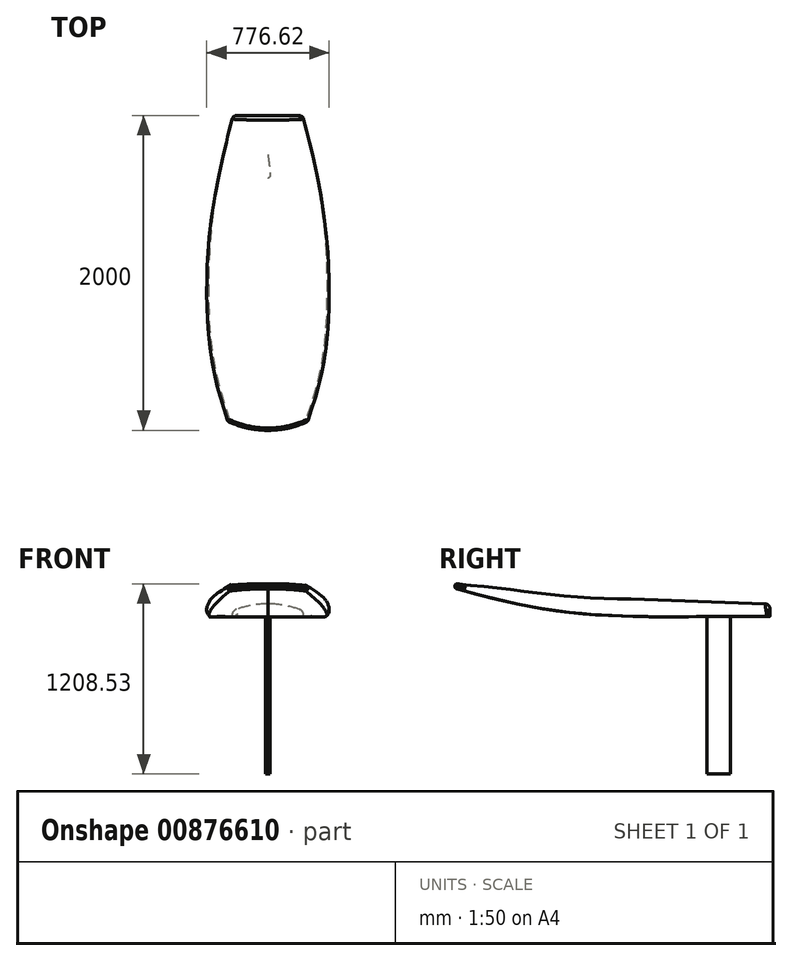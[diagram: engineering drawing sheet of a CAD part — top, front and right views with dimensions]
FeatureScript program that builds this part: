
annotation { "Feature Type Name" : "Feature", "Feature Type Description" : "" }
export const myFeature = defineFeature(function(context is Context, id is Id, definition is map)
    precondition{}
    {
        {
            var Q0;
            Q0=qCreatedBy(makeId("Right.planeOp"),FACE);
            var sketch = newSketch(context, id + "F0", { "sketchPlane" : qUnion([Q0])});
            skLineSegment(sketch, "E0", {"start": v(400, 0) * mm, "end": v(-400, 0) * mm, "construction": true});
            skLineSegment(sketch, "E1", {"start": v(-1600, 0) * mm, "end": v(-1600, 210) * mm, "construction": true});
            skLineSegment(sketch, "E2", {"start": v(-1600, 210) * mm, "end": v(400, 210) * mm, "construction": true});
            skLineSegment(sketch, "E3", {"start": v(400, 210) * mm, "end": v(400, 0) * mm, "construction": true});
            skArc(sketch, "E4", {"start": v(-1600, 180) * mm, "mid": v(-1006.71, 45.25) * mm, "end": v(-400, 0) * mm});
            skLineSegment(sketch, "E5", {"start": v(0, 0) * mm, "end": v(0, -1000) * mm});
            skLineSegment(sketch, "E6", {"start": v(150, 0) * mm, "end": v(150, -1000) * mm});
            skLineSegment(sketch, "E7", {"start": v(-200, -1000) * mm, "end": v(600, -1000) * mm});
            skLineSegment(sketch, "E8", {"start": v(400, 80) * mm, "end": v(-290.38, 105) * mm});
            skPoint(sketch, "E8.endSnap0", {"position": v(400, 105) * mm});
            skArc(sketch, "E9", {"start": v(-1600, 210) * mm, "mid": v(-946.34, 143.15) * mm, "end": v(-290.38, 105) * mm});
            skPoint(sketch, "E10", {"position": v(200, 0) * mm});
            skPoint(sketch, "E11", {"position": v(-200, 0) * mm});
            skPoint(sketch, "E12", {"position": v(-600, 4.9) * mm});
            skPoint(sketch, "E13", {"position": v(-800, 19.6) * mm});
            skPoint(sketch, "E14", {"position": v(-1000, 44.25) * mm});
            skPoint(sketch, "E15", {"position": v(-1200, 79) * mm});
            skPoint(sketch, "E16", {"position": v(-1400, 124.13) * mm});
            skLineSegment(sketch, "E17", {"start": v(400, 10) * mm, "end": v(-421.1, 30) * mm, "construction": true});
            skArc(sketch, "E18", {"start": v(-1600, 195) * mm, "mid": v(-1015.29, 78.66) * mm, "end": v(-421.1, 30) * mm, "construction": true});
            skLineSegment(sketch, "E19", {"start": v(400, 70) * mm, "end": v(-600, 93.11) * mm});
            skArc(sketch, "E20", {"start": v(-600, 93.11) * mm, "mid": v(-1101.55, 81.85) * mm, "end": v(-1600, 25) * mm});
            skPoint(sketch, "E21", {"position": v(-400, 108.97) * mm});
            skSolve(sketch);
        }
        {
            var Q0;
            Q0=qCreatedBy(makeId("Top.planeOp"),FACE);
            var sketch = newSketch(context, id + "F1", { "sketchPlane" : qUnion([Q0])});
            skLineSegment(sketch, "E22.left", {"start": v(0, 400) * mm, "end": v(0, -1600) * mm});
            skLineSegment(sketch, "E23.bottom", {"start": v(375, -1600) * mm, "end": v(-375, -1600) * mm});
            skLineSegment(sketch, "E23.top", {"start": v(375, 400) * mm, "end": v(-375, 400) * mm});
            skLineSegment(sketch, "E23.left", {"start": v(375, -1600) * mm, "end": v(375, 400) * mm});
            skLineSegment(sketch, "E23.right", {"start": v(-375, -1600) * mm, "end": v(-375, 400) * mm});
            skFitSpline(sketch, "E24", {"points": [v(220, 400) * mm, v(350, -250) * mm, v(350, -1100) * mm, v(220, -1600) * mm], "startDerivative": vector(542.74, -2261.4) * mm, "endDerivative": vector(-470.53, -717.24) * mm});
            skFitSpline(sketch, "E25", {"points": [v(0, 150) * mm, v(-12, 40) * mm, v(-10, 12.5) * mm, v(0, 0) * mm], "startDerivative": vector(-33.83, -253.74) * mm, "endDerivative": vector(59.3, -29.65) * mm});
            skArc(sketch, "E26", {"start": v(0, -1600) * mm, "mid": v(198.71, -1566.14) * mm, "end": v(375, -1468.37) * mm});
            skSolve(sketch);
        }
        {
            var Q0;
            Q0=sQuery(id+"F1.wireOp",EDGE,"E23.top");
            cPoint(context, id + "F2", {"entities" : qUnion([Q0]), "parameter" : 0.5});
        }
        {
            var Q0;
            Q0 = qCreatedBy(id + "F2" ,VERTEX);
            var Q1;
            Q1=qCreatedBy(makeId("Front.planeOp"),FACE);
            cPlane(context, id + "F3", {"entities" : qUnion([Q0, Q1]), "cplaneType" : CPlaneType.PLANE_POINT, "offset" : 25 * mm, "width" : 150 * mm, "height" : 150 * mm});
        }
        {
            var Q0;
            Q0=qCreatedBy(makeId("Front.planeOp"),FACE);
            var Q1;
            Q1=sQuery(id+"F0.wireOp",VERTEX,"E5.start");
            cPlane(context, id + "F4", {"entities" : qUnion([Q0, Q1]), "cplaneType" : CPlaneType.PLANE_POINT, "offset" : 25 * mm, "width" : 150 * mm, "height" : 150 * mm});
        }
        {
            var Q0;
            Q0=qCreatedBy(makeId("Front.planeOp"),FACE);
            var Q1;
            Q1=sQuery(id+"F0.wireOp",VERTEX,"E4.end");
            cPlane(context, id + "F5", {"entities" : qUnion([Q0, Q1]), "cplaneType" : CPlaneType.PLANE_POINT, "offset" : 25 * mm, "width" : 150 * mm, "height" : 150 * mm});
        }
        {
            var Q0;
            Q0=qCreatedBy(makeId("Front.planeOp"),FACE);
            var Q1;
            Q1=sQuery(id+"F0.wireOp",VERTEX,"E13");
            cPlane(context, id + "F6", {"entities" : qUnion([Q0, Q1]), "cplaneType" : CPlaneType.PLANE_POINT, "offset" : 25 * mm, "width" : 150 * mm, "height" : 150 * mm});
        }
        {
            var Q0;
            Q0=qCreatedBy(makeId("Front.planeOp"),FACE);
            var Q1;
            Q1=sQuery(id+"F0.wireOp",VERTEX,"E15");
            cPlane(context, id + "F7", {"entities" : qUnion([Q0, Q1]), "cplaneType" : CPlaneType.PLANE_POINT, "offset" : 25 * mm, "width" : 150 * mm, "height" : 150 * mm});
        }
        {
            var Q0;
            Q0=sQuery(id+"F0.wireOp",VERTEX,"E4.start");
            var Q1;
            Q1=qCreatedBy(makeId("Front.planeOp"),FACE);
            cPlane(context, id + "F8", {"entities" : qUnion([Q0, Q1]), "cplaneType" : CPlaneType.PLANE_POINT, "offset" : 25 * mm, "width" : 150 * mm, "height" : 150 * mm});
        }
        {
            var Q0;
            Q0=qCreatedBy(id+"F3.planeOp",FACE);
            var sketch = newSketch(context, id + "F9", { "sketchPlane" : qUnion([Q0])});
            skLineSegment(sketch, "E27", {"start": v(0, 0) * mm, "end": v(220, 0) * mm});
            skArc(sketch, "E28", {"start": v(199.15, 42.62) * mm, "mid": v(101.31, 70.57) * mm, "end": v(0, 80) * mm});
            skArc(sketch, "E29", {"start": v(220, 0) * mm, "mid": v(217.9, 25.38) * mm, "end": v(199.15, 42.62) * mm});
            skLineSegment(sketch, "E30", {"start": v(0, 0) * mm, "end": v(0, 80) * mm});
            skLineSegment(sketch, "E31", {"start": v(186.46, 10) * mm, "end": v(0, 10) * mm, "construction": true});
            skArc(sketch, "E32", {"start": v(0, 0) * mm, "mid": v(35, 35) * mm, "end": v(0, 70) * mm, "construction": true});
            skSolve(sketch);
        }
        {
            var Q0;
            Q0=qCreatedBy(id+"F4.planeOp",FACE);
            var sketch = newSketch(context, id + "F10", { "sketchPlane" : qUnion([Q0])});
            skLineSegment(sketch, "E33", {"start": v(0, 0) * mm, "end": v(310.81, 0) * mm});
            skArc(sketch, "E34", {"start": v(310.81, 0) * mm, "mid": v(312.98, 35.1) * mm, "end": v(286.37, 58.1) * mm});
            skArc(sketch, "E35", {"start": v(286.37, 58.1) * mm, "mid": v(144.33, 85.35) * mm, "end": v(0, 94.48) * mm});
            skLineSegment(sketch, "E36", {"start": v(0, 0) * mm, "end": v(0, 94.48) * mm});
            skLineSegment(sketch, "E37", {"start": v(276.46, 19.74) * mm, "end": v(0, 19.74) * mm, "construction": true});
            skArc(sketch, "E38", {"start": v(0, 79.24) * mm, "mid": v(39.62, 39.62) * mm, "end": v(0, 0) * mm, "construction": true});
            skSolve(sketch);
        }
        {
            var Q0;
            Q0=qCreatedBy(id+"F5.planeOp",FACE);
            var sketch = newSketch(context, id + "F11", { "sketchPlane" : qUnion([Q0])});
            skLineSegment(sketch, "E39", {"start": v(0, 0) * mm, "end": v(364.34, 0) * mm});
            skArc(sketch, "E40", {"start": v(364.34, 0) * mm, "mid": v(373.43, 43.18) * mm, "end": v(340.66, 72.74) * mm});
            skArc(sketch, "E41", {"start": v(340.66, 72.74) * mm, "mid": v(171.3, 99.89) * mm, "end": v(0, 108.97) * mm});
            skLineSegment(sketch, "E42", {"start": v(0, 0) * mm, "end": v(0, 108.97) * mm});
            skLineSegment(sketch, "E43", {"start": v(331.36, 29.49) * mm, "end": v(0, 29.49) * mm, "construction": true});
            skArc(sketch, "E44", {"start": v(0, 0) * mm, "mid": v(44.24, 44.24) * mm, "end": v(0, 88.49) * mm, "construction": true});
            skSolve(sketch);
        }
        {
            var Q0;
            Q0=qCreatedBy(id+"F6.planeOp",FACE);
            var sketch = newSketch(context, id + "F12", { "sketchPlane" : qUnion([Q0])});
            skLineSegment(sketch, "E45", {"start": v(0, 19.6) * mm, "end": v(373.23, 19.6) * mm});
            skLineSegment(sketch, "E46", {"start": v(373.23, 19.6) * mm, "end": v(373.23, 0) * mm, "construction": true});
            skArc(sketch, "E47", {"start": v(346.6, 99.7) * mm, "mid": v(173.7, 117.5) * mm, "end": v(0, 123.45) * mm});
            skLineSegment(sketch, "E48", {"start": v(340.18, 53.09) * mm, "end": v(0, 53.09) * mm, "construction": true});
            skLineSegment(sketch, "E49", {"start": v(0, 19.6) * mm, "end": v(0, 123.45) * mm});
            skArc(sketch, "E50", {"start": v(373.23, 19.6) * mm, "mid": v(384.82, 67.94) * mm, "end": v(346.6, 99.7) * mm});
            skArc(sketch, "E51", {"start": v(0, 0) * mm, "mid": v(47.05, 47.05) * mm, "end": v(0, 94.1) * mm, "construction": true});
            skSolve(sketch);
        }
        {
            var Q0;
            Q0=qCreatedBy(id+"F7.planeOp",FACE);
            var sketch = newSketch(context, id + "F13", { "sketchPlane" : qUnion([Q0])});
            skLineSegment(sketch, "E52", {"start": v(0, 79) * mm, "end": v(335.21, 79) * mm});
            skArc(sketch, "E53", {"start": v(335.21, 79) * mm, "mid": v(347.66, 117.93) * mm, "end": v(316.8, 144.7) * mm});
            skArc(sketch, "E54", {"start": v(316.8, 144.7) * mm, "mid": v(158.74, 160.42) * mm, "end": v(0, 165.66) * mm});
            skLineSegment(sketch, "E55", {"start": v(0, 79) * mm, "end": v(0, 165.66) * mm});
            skArc(sketch, "E56", {"start": v(0, 0) * mm, "mid": v(37.13, 37.13) * mm, "end": v(0, 74.26) * mm, "construction": true});
            skLineSegment(sketch, "E57", {"start": v(311.9, 107.9) * mm, "end": v(0, 107.9) * mm, "construction": true});
            skLineSegment(sketch, "E58", {"start": v(335.21, 79) * mm, "end": v(335.21, 0) * mm, "construction": true});
            skSolve(sketch);
        }
        {
            var Q0;
            Q0=qCreatedBy(id+"F8.planeOp",FACE);
            var sketch = newSketch(context, id + "F14", { "sketchPlane" : qUnion([Q0])});
            skLineSegment(sketch, "E59", {"start": v(0, 180) * mm, "end": v(220, 180) * mm});
            skLineSegment(sketch, "E60", {"start": v(220, 180) * mm, "end": v(220, 0) * mm, "construction": true});
            skLineSegment(sketch, "E61", {"start": v(0, 210) * mm, "end": v(0, 180) * mm});
            skLineSegment(sketch, "E62", {"start": v(0, 210) * mm, "end": v(220, 210) * mm});
            skArc(sketch, "E63", {"start": v(220, 180) * mm, "mid": v(235, 195) * mm, "end": v(220, 210) * mm});
            skSolve(sketch);
        }
        {
            var Q0;
            Q0=sQuery(id+"F1.wireOp",EDGE,"E24");
            var Q1;
            Q1=makeQuery(id+"F9.imprint","IMPRINT",FACE,{"disambiguationData":[TD([[makeQuery(id+"F9.imprint","IMPRINT",EDGE,{"derivedFrom":sQuery(id+"F9.wireOp",EDGE,"E27")}),1.0]])]});
            var Q2;
            Q2=makeQuery(id+"F10.imprint","IMPRINT",FACE,{"disambiguationData":[TD([[makeQuery(id+"F10.imprint","IMPRINT",EDGE,{"derivedFrom":sQuery(id+"F10.wireOp",EDGE,"E33")}),1.0]])]});
            var Q3;
            Q3=makeQuery(id+"F11.imprint","IMPRINT",FACE,{"disambiguationData":[TD([[makeQuery(id+"F11.imprint","IMPRINT",EDGE,{"derivedFrom":sQuery(id+"F11.wireOp",EDGE,"E39")}),1.0]])]});
            var Q4;
            Q4=makeQuery(id+"F12.imprint","IMPRINT",FACE,{"disambiguationData":[TD([[makeQuery(id+"F12.imprint","IMPRINT",EDGE,{"derivedFrom":sQuery(id+"F12.wireOp",EDGE,"E45")}),1.0]])]});
            var Q5;
            Q5=makeQuery(id+"F13.imprint","IMPRINT",FACE,{"disambiguationData":[TD([[makeQuery(id+"F13.imprint","IMPRINT",EDGE,{"derivedFrom":sQuery(id+"F13.wireOp",EDGE,"E52")}),1.0]])]});
            var Q6;
            Q6=makeQuery(id+"F14.imprint","IMPRINT",FACE,{"disambiguationData":[TD([[makeQuery(id+"F14.imprint","IMPRINT",EDGE,{"derivedFrom":sQuery(id+"F14.wireOp",EDGE,"E59")}),1.0]])]});
            var Q7;
            Q7 = qConstructionFilter(qBodyType(qCreatedBy(id + "F9" ,EDGE), BodyType.WIRE), ConstructionObject.NO);
            var Q8;
            Q8 = qConstructionFilter(qBodyType(qCreatedBy(id + "F10" ,EDGE), BodyType.WIRE), ConstructionObject.NO);
            var Q9;
            Q9 = qConstructionFilter(qBodyType(qCreatedBy(id + "F11" ,EDGE), BodyType.WIRE), ConstructionObject.NO);
            var Q10;
            Q10 = qConstructionFilter(qBodyType(qCreatedBy(id + "F12" ,EDGE), BodyType.WIRE), ConstructionObject.NO);
            var Q11;
            Q11 = qConstructionFilter(qBodyType(qCreatedBy(id + "F13" ,EDGE), BodyType.WIRE), ConstructionObject.NO);
            var Q12;
            Q12 = qConstructionFilter(qBodyType(qCreatedBy(id + "F14" ,EDGE), BodyType.WIRE), ConstructionObject.NO);
            var Q13;
            Q13=sQuery(id+"F1.wireOp",VERTEX,"E24.start");
            var Q14;
            Q14=sQuery(id+"F10.wireOp",VERTEX,"E33.end");
            var Q15;
            Q15=sQuery(id+"F11.wireOp",VERTEX,"E39.end");
            var Q16;
            Q16=sQuery(id+"F12.wireOp",VERTEX,"E45.end");
            var Q17;
            Q17=sQuery(id+"F13.wireOp",VERTEX,"E52.end");
            var Q18;
            Q18=sQuery(id+"F14.wireOp",VERTEX,"E59.end");
            loft(context, id + "F15", {"spine" : qUnion([Q0]), "sheetProfilesArray" : [{ "sheetProfileEntities" : qUnion([Q1]) }, { "sheetProfileEntities" : qUnion([Q2]) }, { "sheetProfileEntities" : qUnion([Q3]) }, { "sheetProfileEntities" : qUnion([Q4]) }, { "sheetProfileEntities" : qUnion([Q5]) }, { "sheetProfileEntities" : qUnion([Q6]) }], "wireProfilesArray" : [{ "wireProfileEntities" : qUnion([Q7]) }, { "wireProfileEntities" : qUnion([Q8]) }, { "wireProfileEntities" : qUnion([Q9]) }, { "wireProfileEntities" : qUnion([Q10]) }, { "wireProfileEntities" : qUnion([Q11]) }, { "wireProfileEntities" : qUnion([Q12]) }], "connections" : [{ "connectionEntities" : qUnion([Q13, Q14, Q15, Q16, Q17, Q18]), "connectionEdgeQueries" : qUnion([]), "connectionEdgeParameters" : [] }]});
        }
        {
            var Q0;
            {var subQ0=sQuery(id+"F1.wireOp",EDGE,"E23.left");var subQ1=sQuery(id+"F1.wireOp",EDGE,"E23.bottom");var subQ2=makeQuery(id+"F1.imprint","INTERSECT",VERTEX,{"derivedFrom":[subQ1,subQ0]});Q0=makeQuery(id+"F1.imprint","IMPRINT",FACE,{"disambiguationData":[TD([[makeQuery(id+"F1.imprint","IMPRINT",EDGE,{"disambiguationData":[TD([[subQ2,-1.0]])],"derivedFrom":subQ1}),-1.0]])]});}
            var Q1;
            {var subQ1=sQuery(id+"F1.wireOp",EDGE,"E23.bottom");var subQ3=sQuery(id+"F1.wireOp",EDGE,"E24");var subQ4=makeQuery(id+"F1.imprint","INTERSECT",VERTEX,{"derivedFrom":[subQ1,subQ3]});Q1=makeQuery(id+"F1.imprint","IMPRINT",FACE,{"disambiguationData":[TD([[makeQuery(id+"F1.imprint","IMPRINT",EDGE,{"disambiguationData":[TD([[subQ4,1.0]])],"derivedFrom":subQ3}),-1.0]])]});}
            extrude(context, id + "F16", {"entities" : qUnion([Q0, Q1]), "operationType" : NewBodyOperationType.REMOVE, "endBound" : BoundingType.THROUGH_ALL, "depth" : 25 * mm, "offsetDistance" : 25 * mm});
        }
        {
            var Q0;
            Q0=makeQuery(id+"F15.opLoft","SWEPT_BODY",BODY,{"disambiguationData":[OSD([makeQuery(id+"F9.imprint","IMPRINT",FACE,{"disambiguationData":[TD([[makeQuery(id+"F9.imprint","IMPRINT",EDGE,{"derivedFrom":sQuery(id+"F9.wireOp",EDGE,"E27")}),1.0]])]}),sQuery(id+"F10.wireOp",EDGE,"E34"),sQuery(id+"F11.wireOp",EDGE,"E40"),sQuery(id+"F12.wireOp",EDGE,"E49"),sQuery(id+"F13.wireOp",EDGE,"E53"),makeQuery(id+"F14.imprint","IMPRINT",FACE,{"disambiguationData":[TD([[makeQuery(id+"F14.imprint","IMPRINT",EDGE,{"derivedFrom":sQuery(id+"F14.wireOp",EDGE,"E59")}),1.0]])]})])]});
            var Q1;
            Q1=makeQuery(id+"F15.opLoft","SWEPT_FACE",FACE,{"disambiguationData":[OSD([sQuery(id+"F9.wireOp",EDGE,"E27"),sQuery(id+"F9.wireOp",EDGE,"E28"),sQuery(id+"F9.wireOp",EDGE,"E30"),sQuery(id+"F10.wireOp",EDGE,"E33"),sQuery(id+"F10.wireOp",EDGE,"E35"),sQuery(id+"F10.wireOp",EDGE,"E36"),sQuery(id+"F11.wireOp",EDGE,"E39"),sQuery(id+"F11.wireOp",EDGE,"E41"),sQuery(id+"F11.wireOp",EDGE,"E42"),sQuery(id+"F12.wireOp",EDGE,"E45"),sQuery(id+"F12.wireOp",EDGE,"E47"),sQuery(id+"F12.wireOp",EDGE,"E49"),sQuery(id+"F13.wireOp",EDGE,"E52"),sQuery(id+"F13.wireOp",EDGE,"E54"),sQuery(id+"F13.wireOp",EDGE,"E55"),sQuery(id+"F14.wireOp",EDGE,"E59"),sQuery(id+"F14.wireOp",EDGE,"E61"),sQuery(id+"F14.wireOp",EDGE,"E62")])]});
            mirror(context, id + "F17", {"operationType" : NewBodyOperationType.ADD, "entities" : qUnion([Q0]), "mirrorPlane" : qUnion([Q1])});
        }
        {
            var Q0;
            Q0=qCreatedBy(makeId("Top.planeOp"),FACE);
            var sketch = newSketch(context, id + "F18", { "sketchPlane" : qUnion([Q0])});
            skFitSpline(sketch, "E64.0", {"points": [v(0, 150) * mm, v(-6, 105) * mm, v(-12.66, 44.08) * mm, v(-12.88, 13.55) * mm, v(-4, 2) * mm, v(0, 0) * mm]});
            skFitSpline(sketch, "E65.MirrorCS", {"points": [v(0, 150) * mm, v(6, 105) * mm, v(12.66, 44.08) * mm, v(12.88, 13.55) * mm, v(4, 2) * mm, v(0, 0) * mm]});
            skSolve(sketch);
        }
        {
            var Q0;
            Q0 = qSketchRegion(id + "F18", true);
            var Q1;
            Q1=sQuery(id+"F0.wireOp",VERTEX,"E5.end");
            extrude(context, id + "F19", {"entities" : qUnion([Q0]), "endBound" : BoundingType.UP_TO_VERTEX, "oppositeDirection" : true, "depth" : 25 * mm, "endBoundEntityVertex" : qUnion([Q1]), "offsetDistance" : 25 * mm});
        }
        {
            var Q0;
            Q0=makeQuery(id+"F15.opLoft","MID_CAP_EDGE",EDGE,{"disambiguationData":[OSD([sQuery(id+"F9.wireOp",EDGE,"E28"),sQuery(id+"F9.wireOp",EDGE,"E29"),sQuery(id+"F9.wireOp",EDGE,"E30")])],"capPos":0.0});
            var Q1;
            Q1=makeQuery(id+"F15.opLoft","MID_CAP_EDGE",EDGE,{"disambiguationData":[OSD([sQuery(id+"F9.wireOp",EDGE,"E27"),sQuery(id+"F9.wireOp",EDGE,"E28"),sQuery(id+"F9.wireOp",EDGE,"E29")])],"capPos":0.0});
            var Q2;
            Q2=makeQuery(id+"F17.opPattern","COPY",EDGE,{"derivedFrom":makeQuery(id+"F15.opLoft","MID_CAP_EDGE",EDGE,{"disambiguationData":[OSD([sQuery(id+"F9.wireOp",EDGE,"E28"),sQuery(id+"F9.wireOp",EDGE,"E29"),sQuery(id+"F9.wireOp",EDGE,"E30")])],"capPos":0.0}),"instanceName":"1"});
            var Q3;
            Q3=makeQuery(id+"F17.opPattern","COPY",EDGE,{"derivedFrom":makeQuery(id+"F15.opLoft","MID_CAP_EDGE",EDGE,{"disambiguationData":[OSD([sQuery(id+"F9.wireOp",EDGE,"E27"),sQuery(id+"F9.wireOp",EDGE,"E28"),sQuery(id+"F9.wireOp",EDGE,"E29")])],"capPos":0.0}),"instanceName":"1"});
            fillet(context, id + "F20", {"entities" : qUnion([Q0, Q1, Q2, Q3]), "radius" : 30 * mm, "allowEdgeOverflow" : false});
        }
        {
            var Q0;
            {var subQ0=makeQuery(id+"F16.boolean.opBoolean","COPY",FACE,{"derivedFrom":makeQuery(id+"F16.opExtrude","SWEPT_FACE",FACE,{"disambiguationData":[OSD([sQuery(id+"F1.wireOp",EDGE,"E26")])]})});Q0=makeQuery(id+"F17.boolean.opBoolean","MERGE",FACE,{"derivedFrom":[subQ0,makeQuery(id+"F17.opPattern","COPY",FACE,{"derivedFrom":subQ0,"instanceName":"1"})]});}
            fillet(context, id + "F21", {"entities" : qUnion([Q0]), "radius" : 13 * mm, "tangentPropagation" : true, "allowEdgeOverflow" : false});
        }
    });
